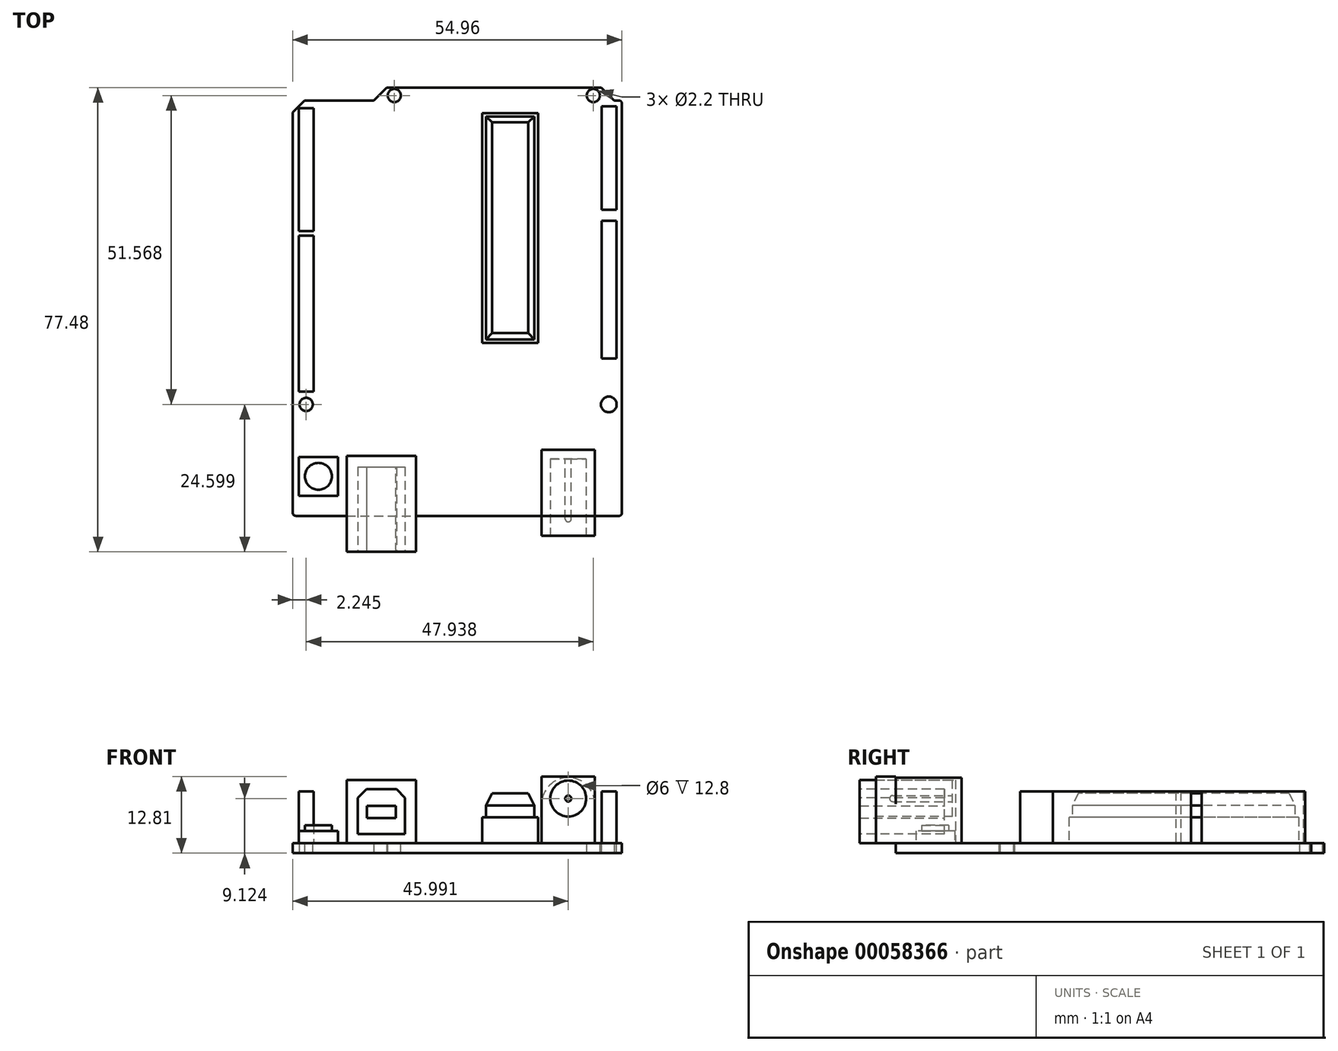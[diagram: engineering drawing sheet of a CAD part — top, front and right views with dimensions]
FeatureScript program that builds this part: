
annotation { "Feature Type Name" : "Feature", "Feature Type Description" : "" }
export const myFeature = defineFeature(function(context is Context, id is Id, definition is map)
    precondition{}
    {
        {
            var Q0;
            Q0=qCreatedBy(makeId("Top.planeOp"),FACE);
            var sketch = newSketch(context, id + "F0", { "sketchPlane" : qUnion([Q0])});
            skLineSegment(sketch, "E0.rect.bottom", {"start": v(-11.81, 35.74) * mm, "end": v(24.03, 35.74) * mm});
            skLineSegment(sketch, "E0.rect.top", {"start": v(-26.94, -35.74) * mm, "end": v(26.97, -35.74) * mm});
            skLineSegment(sketch, "E0.rect.left", {"start": v(-27.48, 31.62) * mm, "end": v(-27.48, -35.2) * mm});
            skLineSegment(sketch, "E0.rect.right", {"start": v(27.48, 33.07) * mm, "end": v(27.48, -35.23) * mm});
            skPoint(sketch, "E0.rect.middle", {"position": v(0, 0) * mm});
            skLineSegment(sketch, "E1.top", {"start": v(-25.49, 33.6) * mm, "end": v(-13.95, 33.6) * mm});
            skPoint(sketch, "E2.orphan", {"position": v(-27.48, 35.74) * mm});
            skLineSegment(sketch, "E3", {"start": v(-27.48, 31.62) * mm, "end": v(-25.49, 33.6) * mm});
            skLineSegment(sketch, "E4", {"start": v(-11.81, 35.74) * mm, "end": v(-13.95, 33.6) * mm});
            skLineSegment(sketch, "E5.top", {"start": v(26.17, 33.6) * mm, "end": v(26.94, 33.6) * mm});
            skLineSegment(sketch, "E6", {"start": v(24.03, 35.74) * mm, "end": v(26.17, 33.6) * mm});
            skPoint(sketch, "E7.orphan", {"position": v(27.48, 35.74) * mm});
            skPoint(sketch, "E8.visualSharp", {"position": v(27.48, -35.74) * mm});
            skArc(sketch, "E8.filletArc", {"start": v(26.97, -35.74) * mm, "mid": v(27.33, -35.6) * mm, "end": v(27.48, -35.23) * mm});
            skPoint(sketch, "E9.visualSharp", {"position": v(27.48, 33.6) * mm});
            skArc(sketch, "E9.filletArc", {"start": v(27.48, 33.07) * mm, "mid": v(27.32, 33.45) * mm, "end": v(26.94, 33.6) * mm});
            skPoint(sketch, "E10.visualSharp", {"position": v(-27.48, -35.74) * mm});
            skArc(sketch, "E10.filletArc", {"start": v(-27.48, -35.2) * mm, "mid": v(-27.32, -35.59) * mm, "end": v(-26.94, -35.74) * mm});
            skPoint(sketch, "E11.second.point", {"position": v(21.12, -10.57) * mm});
            skPoint(sketch, "E11.third.point", {"position": v(22.07, -8.93) * mm});
            skLineSegment(sketch, "E12", {"start": v(-13.95, 33.6) * mm, "end": v(31.22, 33.6) * mm, "construction": true});
            skSolve(sketch);
        }
        {
            var Q0;
            Q0=makeQuery(id+"F0.imprint","IMPRINT",FACE,{"disambiguationData":[TD([[makeQuery(id+"F0.imprint","IMPRINT",EDGE,{"derivedFrom":sQuery(id+"F0.wireOp",EDGE,"E0.rect.bottom")}),-1.0]])]});
            extrude(context, id + "F1", {"entities" : qUnion([Q0]), "depth" : 1.69 * mm});
        }
        {
            var Q0;
            Q0=makeQuery(id+"F1.opExtrude","CAP_FACE",FACE,{"disambiguationData":[OSD([sQuery(id+"F0.wireOp",EDGE,"E0.rect.bottom"),sQuery(id+"F0.wireOp",EDGE,"E0.rect.top"),sQuery(id+"F0.wireOp",EDGE,"E0.rect.left"),sQuery(id+"F0.wireOp",EDGE,"E0.rect.right"),sQuery(id+"F0.wireOp",EDGE,"E1.top"),sQuery(id+"F0.wireOp",EDGE,"E3"),sQuery(id+"F0.wireOp",EDGE,"E4"),sQuery(id+"F0.wireOp",EDGE,"E5.top"),sQuery(id+"F0.wireOp",EDGE,"E6"),sQuery(id+"F0.wireOp",EDGE,"E8.filletArc"),sQuery(id+"F0.wireOp",EDGE,"E9.filletArc"),sQuery(id+"F0.wireOp",EDGE,"E10.filletArc")])],"isStart":false});
            var sketch = newSketch(context, id + "F2", { "sketchPlane" : qUnion([Q0])});
            skLineSegment(sketch, "E13.top", {"start": v(24.1, -9.48) * mm, "end": v(26.53, -9.48) * mm});
            skLineSegment(sketch, "E13.left", {"start": v(24.1, 32.6) * mm, "end": v(24.1, 15.32) * mm});
            skLineSegment(sketch, "E13.right", {"start": v(26.53, 32.6) * mm, "end": v(26.53, 15.32) * mm});
            skLineSegment(sketch, "E14", {"start": v(24.1, 32.6) * mm, "end": v(26.53, 32.6) * mm});
            skLineSegment(sketch, "E15", {"start": v(24.1, 15.32) * mm, "end": v(26.53, 15.32) * mm});
            skLineSegment(sketch, "E16", {"start": v(24.1, 13.52) * mm, "end": v(26.53, 13.52) * mm});
            skLineSegment(sketch, "E17.trimOffspring", {"start": v(24.1, 13.52) * mm, "end": v(24.1, -9.48) * mm});
            skLineSegment(sketch, "E18.trimOffspring", {"start": v(26.53, 13.52) * mm, "end": v(26.53, -9.48) * mm});
            skLineSegment(sketch, "E19.bottom", {"start": v(-26.48, 32.3) * mm, "end": v(-23.98, 32.3) * mm});
            skLineSegment(sketch, "E19.top", {"start": v(-26.48, -14.99) * mm, "end": v(-23.98, -14.99) * mm});
            skLineSegment(sketch, "E19.left", {"start": v(-26.48, 32.3) * mm, "end": v(-26.48, 11.81) * mm});
            skLineSegment(sketch, "E19.right", {"start": v(-23.98, 32.3) * mm, "end": v(-23.98, 11.81) * mm});
            skLineSegment(sketch, "E20.bottom", {"start": v(-26.48, 11.81) * mm, "end": v(-23.98, 11.81) * mm});
            skLineSegment(sketch, "E20.top", {"start": v(-26.48, 11.01) * mm, "end": v(-23.98, 11.01) * mm});
            skLineSegment(sketch, "E21.trimOffspring", {"start": v(-23.98, 11.01) * mm, "end": v(-23.98, -14.99) * mm});
            skLineSegment(sketch, "E22.trimOffspring", {"start": v(-26.48, 11.01) * mm, "end": v(-26.48, -14.99) * mm});
            skSolve(sketch);
        }
        {
            var Q0;
            Q0=makeQuery(id+"F2.imprint","IMPRINT",FACE,{"disambiguationData":[TD([[makeQuery(id+"F2.imprint","IMPRINT",EDGE,{"derivedFrom":sQuery(id+"F2.wireOp",EDGE,"E13.top")}),1.0]])]});
            var Q1;
            Q1=makeQuery(id+"F2.imprint","IMPRINT",FACE,{"disambiguationData":[TD([[makeQuery(id+"F2.imprint","IMPRINT",EDGE,{"derivedFrom":sQuery(id+"F2.wireOp",EDGE,"E13.left")}),1.0]])]});
            var Q2;
            Q2=makeQuery(id+"F2.imprint","IMPRINT",FACE,{"disambiguationData":[TD([[makeQuery(id+"F2.imprint","IMPRINT",EDGE,{"derivedFrom":sQuery(id+"F2.wireOp",EDGE,"E19.bottom")}),-1.0]])]});
            var Q3;
            Q3=makeQuery(id+"F2.imprint","IMPRINT",FACE,{"disambiguationData":[TD([[makeQuery(id+"F2.imprint","IMPRINT",EDGE,{"derivedFrom":sQuery(id+"F2.wireOp",EDGE,"E19.top")}),1.0]])]});
            extrude(context, id + "F3", {"entities" : qUnion([Q0, Q1, Q2, Q3]), "depth" : 8.6 * mm});
        }
        {
            var Q0;
            Q0=makeQuery(id+"F1.opExtrude","SWEPT_FACE",FACE,{"disambiguationData":[OSD([sQuery(id+"F0.wireOp",EDGE,"E0.rect.top")])]});
            cPlane(context, id + "F4", {"entities" : qUnion([Q0]), "cplaneType" : CPlaneType.OFFSET, "offset" : 0 * mm, "width" : 150 * mm, "height" : 150 * mm});
        }
        {
            var Q0;
            Q0=qCreatedBy(id+"F4.planeOp",FACE);
            var sketch = newSketch(context, id + "F5", { "sketchPlane" : qUnion([Q0])});
            skLineSegment(sketch, "E23", {"start": v(30.92, 1.68) * mm, "end": v(22.95, 1.68) * mm, "construction": true});
            skLineSegment(sketch, "E24.bottom", {"start": v(22.95, 1.68) * mm, "end": v(14.07, 1.68) * mm});
            skLineSegment(sketch, "E24.left", {"start": v(22.95, 1.68) * mm, "end": v(22.95, 8.18) * mm});
            skLineSegment(sketch, "E24.right", {"start": v(14.07, 1.68) * mm, "end": v(14.07, 8.18) * mm});
            skArc(sketch, "E25", {"start": v(22.95, 8.18) * mm, "mid": v(18.51, 12.62) * mm, "end": v(14.07, 8.18) * mm});
            skSolve(sketch);
        }
        {
            var Q0;
            Q0=makeQuery(id+"F5.imprint","IMPRINT",FACE,{"disambiguationData":[TD([[makeQuery(id+"F5.imprint","IMPRINT",EDGE,{"derivedFrom":sQuery(id+"F5.wireOp",EDGE,"E24.bottom")}),-1.0]])]});
            extrude(context, id + "F6", {"entities" : qUnion([Q0]), "oppositeDirection" : true, "depth" : 11 * mm});
        }
        {
            var Q0;
            Q0=qCreatedBy(id+"F4.planeOp",FACE);
            var sketch = newSketch(context, id + "F7", { "sketchPlane" : qUnion([Q0])});
            skLineSegment(sketch, "E26.bottom", {"start": v(14.07, 1.69) * mm, "end": v(22.95, 1.69) * mm});
            skLineSegment(sketch, "E26.top", {"start": v(14.07, 12.81) * mm, "end": v(22.95, 12.81) * mm});
            skLineSegment(sketch, "E26.left", {"start": v(14.07, 1.69) * mm, "end": v(14.07, 12.81) * mm});
            skLineSegment(sketch, "E26.right", {"start": v(22.95, 1.69) * mm, "end": v(22.95, 12.81) * mm});
            skSolve(sketch);
        }
        {
            var Q0;
            Q0=makeQuery(id+"F7.imprint","IMPRINT",FACE,{"disambiguationData":[TD([[makeQuery(id+"F7.imprint","IMPRINT",EDGE,{"derivedFrom":sQuery(id+"F7.wireOp",EDGE,"E26.bottom")}),1.0]])]});
            extrude(context, id + "F8", {"entities" : qUnion([Q0]), "operationType" : NewBodyOperationType.ADD, "depth" : 3.3 * mm});
        }
        {
            var Q0;
            Q0=makeQuery(id+"F8.opExtrude","CAP_FACE",FACE,{"disambiguationData":[OSD([sQuery(id+"F7.wireOp",EDGE,"E26.bottom"),sQuery(id+"F7.wireOp",EDGE,"E26.top"),sQuery(id+"F7.wireOp",EDGE,"E26.left"),sQuery(id+"F7.wireOp",EDGE,"E26.right")])],"isStart":false});
            var sketch = newSketch(context, id + "F9", { "sketchPlane" : qUnion([Q0])});
            skCircle(sketch, "E27", {"center": v(18.51, 9.12) * mm, "radius": 3 * mm});
            skSolve(sketch);
        }
        {
            var Q0;
            Q0=makeQuery(id+"F9.imprint","IMPRINT",FACE,{"disambiguationData":[TD([[makeQuery(id+"F9.imprint","IMPRINT",EDGE,{"derivedFrom":sQuery(id+"F9.wireOp",EDGE,"E27")}),1.0]])]});
            var Q1;
            Q1=sQuery(id+"F9.wireOp",EDGE,"E27");
            extrude(context, id + "F10", {"entities" : qUnion([Q0]), "operationType" : NewBodyOperationType.REMOVE, "surfaceEntities" : qUnion([Q1]), "oppositeDirection" : true, "depth" : 12.8 * mm});
        }
        {
            var Q0;
            Q0=makeQuery(id+"F10.boolean.opBoolean","COPY",FACE,{"derivedFrom":makeQuery(id+"F10.opExtrude","CAP_FACE",FACE,{"disambiguationData":[OSD([sQuery(id+"F9.wireOp",EDGE,"E27")])],"isStart":false})});
            var sketch = newSketch(context, id + "F11", { "sketchPlane" : qUnion([Q0])});
            skCircle(sketch, "E28.0", {"center": v(18.51, 9.12) * mm, "radius": 3 * mm});
            skCircle(sketch, "E29", {"center": v(18.51, 9.12) * mm, "radius": 0.5 * mm});
            skSolve(sketch);
        }
        {
            var Q0;
            Q0=makeQuery(id+"F11.imprint","IMPRINT",FACE,{"disambiguationData":[TD([[makeQuery(id+"F11.imprint","IMPRINT",EDGE,{"derivedFrom":sQuery(id+"F11.wireOp",EDGE,"E29")}),1.0]])]});
            var Q1;
            Q1=sQuery(id+"F11.wireOp",EDGE,"E29");
            extrude(context, id + "F12", {"entities" : qUnion([Q0]), "surfaceEntities" : qUnion([Q1]), "depth" : 10 * mm});
        }
        {
            var Q0;
            Q0=makeQuery(id+"F1.opExtrude","CAP_FACE",FACE,{"disambiguationData":[OSD([sQuery(id+"F0.wireOp",EDGE,"E0.rect.bottom"),sQuery(id+"F0.wireOp",EDGE,"E0.rect.top"),sQuery(id+"F0.wireOp",EDGE,"E0.rect.left"),sQuery(id+"F0.wireOp",EDGE,"E0.rect.right"),sQuery(id+"F0.wireOp",EDGE,"E1.top"),sQuery(id+"F0.wireOp",EDGE,"E3"),sQuery(id+"F0.wireOp",EDGE,"E4"),sQuery(id+"F0.wireOp",EDGE,"E5.top"),sQuery(id+"F0.wireOp",EDGE,"E6"),sQuery(id+"F0.wireOp",EDGE,"E8.filletArc"),sQuery(id+"F0.wireOp",EDGE,"E9.filletArc"),sQuery(id+"F0.wireOp",EDGE,"E10.filletArc")])],"isStart":false});
            var sketch = newSketch(context, id + "F13", { "sketchPlane" : qUnion([Q0])});
            skLineSegment(sketch, "E30.bottom", {"start": v(-18.48, -35.74) * mm, "end": v(-6.88, -35.74) * mm});
            skLineSegment(sketch, "E30.top", {"start": v(-18.48, -25.74) * mm, "end": v(-6.88, -25.74) * mm});
            skLineSegment(sketch, "E30.left", {"start": v(-18.48, -35.74) * mm, "end": v(-18.48, -25.74) * mm});
            skLineSegment(sketch, "E30.right", {"start": v(-6.88, -35.74) * mm, "end": v(-6.88, -25.74) * mm});
            skSolve(sketch);
        }
        {
            var Q0;
            Q0=makeQuery(id+"F13.imprint","IMPRINT",FACE,{"disambiguationData":[TD([[makeQuery(id+"F13.imprint","IMPRINT",EDGE,{"derivedFrom":sQuery(id+"F13.wireOp",EDGE,"E30.bottom")}),1.0]])]});
            extrude(context, id + "F14", {"entities" : qUnion([Q0]), "depth" : 10.5 * mm});
        }
        {
            var Q0;
            Q0=makeQuery(id+"F14.opExtrude","SWEPT_FACE",FACE,{"disambiguationData":[OSD([sQuery(id+"F13.wireOp",EDGE,"E30.bottom")])]});
            var sketch = newSketch(context, id + "F15", { "sketchPlane" : qUnion([Q0])});
            skLineSegment(sketch, "E31.bottom", {"start": v(-18.48, 12.2) * mm, "end": v(-6.88, 12.2) * mm});
            skLineSegment(sketch, "E31.top", {"start": v(-18.48, 1.69) * mm, "end": v(-6.88, 1.69) * mm});
            skLineSegment(sketch, "E31.left", {"start": v(-18.48, 12.2) * mm, "end": v(-18.48, 1.69) * mm});
            skLineSegment(sketch, "E31.right", {"start": v(-6.88, 12.2) * mm, "end": v(-6.88, 1.69) * mm});
            skSolve(sketch);
        }
        {
            var Q0;
            Q0=makeQuery(id+"F15.imprint","IMPRINT",FACE,{"disambiguationData":[TD([[makeQuery(id+"F15.imprint","IMPRINT",EDGE,{"derivedFrom":sQuery(id+"F15.wireOp",EDGE,"E31.bottom")}),-1.0]])]});
            extrude(context, id + "F16", {"entities" : qUnion([Q0]), "operationType" : NewBodyOperationType.ADD, "depth" : 6 * mm});
        }
        {
            var Q0;
            Q0=makeQuery(id+"F16.opExtrude","CAP_FACE",FACE,{"disambiguationData":[OSD([sQuery(id+"F15.wireOp",EDGE,"E31.bottom"),sQuery(id+"F15.wireOp",EDGE,"E31.top"),sQuery(id+"F15.wireOp",EDGE,"E31.left"),sQuery(id+"F15.wireOp",EDGE,"E31.right")])],"isStart":false});
            var sketch = newSketch(context, id + "F17", { "sketchPlane" : qUnion([Q0])});
            skLineSegment(sketch, "E32.rect.bottom", {"start": v(-16.63, 3.2) * mm, "end": v(-8.73, 3.2) * mm});
            skLineSegment(sketch, "E32.rect.top", {"start": v(-15.19, 10.7) * mm, "end": v(-10.17, 10.7) * mm});
            skLineSegment(sketch, "E32.rect.left", {"start": v(-16.63, 3.2) * mm, "end": v(-16.63, 9.25) * mm});
            skLineSegment(sketch, "E32.rect.right", {"start": v(-8.73, 3.2) * mm, "end": v(-8.73, 9.25) * mm});
            skPoint(sketch, "E32.rect.middle", {"position": v(-12.68, 6.94) * mm});
            skPoint(sketch, "E32.rect.middle.positionSnap0", {"position": v(-18.48, 6.94) * mm});
            skPoint(sketch, "E32.rect.middle.positionSnap1", {"position": v(-12.68, 12.2) * mm});
            skPoint(sketch, "E32.rect.centerSnap0", {"position": v(-18.48, 6.94) * mm});
            skPoint(sketch, "E32.rect.centerSnap1", {"position": v(-12.68, 12.2) * mm});
            skLineSegment(sketch, "E33", {"start": v(-16.63, 9.25) * mm, "end": v(-15.19, 10.7) * mm});
            skLineSegment(sketch, "E34", {"start": v(-10.17, 10.7) * mm, "end": v(-8.73, 9.25) * mm});
            skPoint(sketch, "E35.orphan", {"position": v(-16.63, 10.7) * mm});
            skPoint(sketch, "E36.orphan", {"position": v(-8.73, 10.7) * mm});
            skSolve(sketch);
        }
        {
            var Q0;
            Q0=makeQuery(id+"F17.imprint","IMPRINT",FACE,{"disambiguationData":[TD([[makeQuery(id+"F17.imprint","IMPRINT",EDGE,{"derivedFrom":sQuery(id+"F17.wireOp",EDGE,"E32.rect.bottom")}),1.0]])]});
            extrude(context, id + "F18", {"entities" : qUnion([Q0]), "operationType" : NewBodyOperationType.REMOVE, "oppositeDirection" : true, "depth" : 14.14 * mm});
        }
        {
            var Q0;
            Q0=makeQuery(id+"F18.boolean.opBoolean","COPY",FACE,{"derivedFrom":makeQuery(id+"F18.opExtrude","CAP_FACE",FACE,{"disambiguationData":[OSD([sQuery(id+"F17.wireOp",EDGE,"E32.rect.bottom"),sQuery(id+"F17.wireOp",EDGE,"E32.rect.top"),sQuery(id+"F17.wireOp",EDGE,"E32.rect.left"),sQuery(id+"F17.wireOp",EDGE,"E32.rect.right"),sQuery(id+"F17.wireOp",EDGE,"E33"),sQuery(id+"F17.wireOp",EDGE,"E34")])],"isStart":false})});
            var sketch = newSketch(context, id + "F19", { "sketchPlane" : qUnion([Q0])});
            skLineSegment(sketch, "E37.rect.bottom", {"start": v(-15.12, 5.84) * mm, "end": v(-10.24, 5.84) * mm});
            skLineSegment(sketch, "E37.rect.top", {"start": v(-15.12, 7.92) * mm, "end": v(-10.24, 7.92) * mm});
            skLineSegment(sketch, "E37.rect.left", {"start": v(-15.12, 5.84) * mm, "end": v(-15.12, 7.92) * mm});
            skLineSegment(sketch, "E37.rect.right", {"start": v(-10.24, 5.84) * mm, "end": v(-10.24, 7.92) * mm});
            skPoint(sketch, "E37.rect.middle", {"position": v(-12.68, 6.88) * mm});
            skPoint(sketch, "E37.rect.middle.positionSnap0", {"position": v(-12.68, 10.7) * mm});
            skPoint(sketch, "E37.rect.centerSnap0", {"position": v(-12.68, 10.7) * mm});
            skSolve(sketch);
        }
        {
            var Q0;
            Q0=qSketchRegion(id+"F19",true);
            var Q1;
            Q1=makeQuery(id+"F16.opExtrude","CAP_FACE",FACE,{"disambiguationData":[OSD([sQuery(id+"F15.wireOp",EDGE,"E31.bottom"),sQuery(id+"F15.wireOp",EDGE,"E31.top"),sQuery(id+"F15.wireOp",EDGE,"E31.left"),sQuery(id+"F15.wireOp",EDGE,"E31.right")])],"isStart":false});
            extrude(context, id + "F20", {"entities" : qUnion([Q0]), "endBound" : BoundingType.UP_TO_SURFACE, "endBoundEntityFace" : qUnion([Q1]), "depth" : 25 * mm});
        }
        {
            var Q0;
            Q0=makeQuery(id+"F1.opExtrude","CAP_FACE",FACE,{"disambiguationData":[OSD([sQuery(id+"F0.wireOp",EDGE,"E0.rect.bottom"),sQuery(id+"F0.wireOp",EDGE,"E0.rect.top"),sQuery(id+"F0.wireOp",EDGE,"E0.rect.left"),sQuery(id+"F0.wireOp",EDGE,"E0.rect.right"),sQuery(id+"F0.wireOp",EDGE,"E1.top"),sQuery(id+"F0.wireOp",EDGE,"E3"),sQuery(id+"F0.wireOp",EDGE,"E4"),sQuery(id+"F0.wireOp",EDGE,"E5.top"),sQuery(id+"F0.wireOp",EDGE,"E6"),sQuery(id+"F0.wireOp",EDGE,"E8.filletArc"),sQuery(id+"F0.wireOp",EDGE,"E9.filletArc"),sQuery(id+"F0.wireOp",EDGE,"E10.filletArc")])],"isStart":false});
            var sketch = newSketch(context, id + "F21", { "sketchPlane" : qUnion([Q0])});
            skLineSegment(sketch, "E38.rect.bottom", {"start": v(-26.44, -25.9) * mm, "end": v(-19.94, -25.9) * mm});
            skLineSegment(sketch, "E38.rect.top", {"start": v(-26.44, -32.4) * mm, "end": v(-19.94, -32.4) * mm});
            skLineSegment(sketch, "E38.rect.left", {"start": v(-26.44, -25.9) * mm, "end": v(-26.44, -32.4) * mm});
            skLineSegment(sketch, "E38.rect.right", {"start": v(-19.94, -25.9) * mm, "end": v(-19.94, -32.4) * mm});
            skPoint(sketch, "E38.rect.middle", {"position": v(-23.19, -29.14) * mm});
            skSolve(sketch);
        }
        {
            var Q0;
            Q0=makeQuery(id+"F21.imprint","IMPRINT",FACE,{"disambiguationData":[TD([[makeQuery(id+"F21.imprint","IMPRINT",EDGE,{"derivedFrom":sQuery(id+"F21.wireOp",EDGE,"E38.rect.bottom")}),-1.0]])]});
            extrude(context, id + "F22", {"entities" : qUnion([Q0]), "depth" : 2 * mm});
        }
        {
            var Q0;
            Q0=makeQuery(id+"F22.opExtrude","CAP_FACE",FACE,{"disambiguationData":[OSD([sQuery(id+"F21.wireOp",EDGE,"E38.rect.bottom"),sQuery(id+"F21.wireOp",EDGE,"E38.rect.top"),sQuery(id+"F21.wireOp",EDGE,"E38.rect.left"),sQuery(id+"F21.wireOp",EDGE,"E38.rect.right")])],"isStart":false});
            var sketch = newSketch(context, id + "F23", { "sketchPlane" : qUnion([Q0])});
            skCircle(sketch, "E39", {"center": v(-23.19, -29.14) * mm, "radius": 2.24 * mm});
            skPoint(sketch, "E39.centerSnap0", {"position": v(-26.44, -29.14) * mm});
            skSolve(sketch);
        }
        {
            var Q0;
            Q0=makeQuery(id+"F23.imprint","IMPRINT",FACE,{"disambiguationData":[TD([[makeQuery(id+"F23.imprint","IMPRINT",EDGE,{"derivedFrom":sQuery(id+"F23.wireOp",EDGE,"E39")}),1.0]])]});
            extrude(context, id + "F24", {"entities" : qUnion([Q0]), "depth" : 1 * mm});
        }
        {
            var Q0;
            Q0=makeQuery(id+"F1.opExtrude","CAP_FACE",FACE,{"disambiguationData":[OSD([sQuery(id+"F0.wireOp",EDGE,"E0.rect.bottom"),sQuery(id+"F0.wireOp",EDGE,"E0.rect.top"),sQuery(id+"F0.wireOp",EDGE,"E0.rect.left"),sQuery(id+"F0.wireOp",EDGE,"E0.rect.right"),sQuery(id+"F0.wireOp",EDGE,"E1.top"),sQuery(id+"F0.wireOp",EDGE,"E3"),sQuery(id+"F0.wireOp",EDGE,"E4"),sQuery(id+"F0.wireOp",EDGE,"E5.top"),sQuery(id+"F0.wireOp",EDGE,"E6"),sQuery(id+"F0.wireOp",EDGE,"E8.filletArc"),sQuery(id+"F0.wireOp",EDGE,"E9.filletArc"),sQuery(id+"F0.wireOp",EDGE,"E10.filletArc")])],"isStart":false});
            var sketch = newSketch(context, id + "F25", { "sketchPlane" : qUnion([Q0])});
            skLineSegment(sketch, "E40.bottom", {"start": v(13.47, 31.5) * mm, "end": v(4.14, 31.5) * mm});
            skLineSegment(sketch, "E40.top", {"start": v(13.47, -6.87) * mm, "end": v(4.14, -6.87) * mm});
            skLineSegment(sketch, "E40.left", {"start": v(13.47, 31.5) * mm, "end": v(13.47, -6.87) * mm});
            skLineSegment(sketch, "E40.right", {"start": v(4.14, 31.5) * mm, "end": v(4.14, -6.87) * mm});
            skSolve(sketch);
        }
        {
            var Q0;
            Q0=makeQuery(id+"F25.imprint","IMPRINT",FACE,{"disambiguationData":[TD([[makeQuery(id+"F25.imprint","IMPRINT",EDGE,{"derivedFrom":sQuery(id+"F25.wireOp",EDGE,"E40.bottom")}),1.0]])]});
            extrude(context, id + "F26", {"entities" : qUnion([Q0]), "depth" : 4.3 * mm});
        }
        {
            var Q0;
            Q0=makeQuery(id+"F26.opExtrude","CAP_FACE",FACE,{"disambiguationData":[OSD([sQuery(id+"F25.wireOp",EDGE,"E40.bottom"),sQuery(id+"F25.wireOp",EDGE,"E40.top"),sQuery(id+"F25.wireOp",EDGE,"E40.left"),sQuery(id+"F25.wireOp",EDGE,"E40.right")])],"isStart":false});
            var sketch = newSketch(context, id + "F27", { "sketchPlane" : qUnion([Q0])});
            skLineSegment(sketch, "E41.rect.bottom", {"start": v(4.76, 30.91) * mm, "end": v(12.84, 30.91) * mm});
            skLineSegment(sketch, "E41.rect.top", {"start": v(4.76, -6.28) * mm, "end": v(12.84, -6.28) * mm});
            skLineSegment(sketch, "E41.rect.left", {"start": v(4.76, 30.91) * mm, "end": v(4.76, -6.28) * mm});
            skLineSegment(sketch, "E41.rect.right", {"start": v(12.84, 30.91) * mm, "end": v(12.84, -6.28) * mm});
            skPoint(sketch, "E41.rect.middle", {"position": v(8.8, 12.32) * mm});
            skPoint(sketch, "E41.rect.middle.positionSnap0", {"position": v(8.8, 31.5) * mm});
            skPoint(sketch, "E41.rect.middle.positionSnap1", {"position": v(4.14, 12.32) * mm});
            skPoint(sketch, "E41.rect.centerSnap0", {"position": v(8.8, 31.5) * mm});
            skPoint(sketch, "E41.rect.centerSnap1", {"position": v(4.14, 12.32) * mm});
            skSolve(sketch);
        }
        {
            var Q0;
            Q0=makeQuery(id+"F27.imprint","IMPRINT",FACE,{"disambiguationData":[TD([[makeQuery(id+"F27.imprint","IMPRINT",EDGE,{"derivedFrom":sQuery(id+"F27.wireOp",EDGE,"E41.rect.bottom")}),-1.0]])]});
            extrude(context, id + "F28", {"entities" : qUnion([Q0]), "depth" : 2 * mm});
        }
        {
            var Q0;
            Q0=makeQuery(id+"F28.opExtrude","CAP_FACE",FACE,{"disambiguationData":[OSD([sQuery(id+"F27.wireOp",EDGE,"E41.rect.bottom"),sQuery(id+"F27.wireOp",EDGE,"E41.rect.top"),sQuery(id+"F27.wireOp",EDGE,"E41.rect.left"),sQuery(id+"F27.wireOp",EDGE,"E41.rect.right")])],"isStart":false});
            cPlane(context, id + "F29", {"entities" : qUnion([Q0]), "cplaneType" : CPlaneType.OFFSET, "offset" : 2 * mm, "width" : 150 * mm, "height" : 150 * mm});
        }
        {
            var Q0;
            Q0=qCreatedBy(id+"F29.planeOp",FACE);
            var sketch = newSketch(context, id + "F30", { "sketchPlane" : qUnion([Q0])});
            skLineSegment(sketch, "E42.bottom", {"start": v(5.78, 29.94) * mm, "end": v(11.83, 29.94) * mm});
            skLineSegment(sketch, "E42.top", {"start": v(5.78, -5.22) * mm, "end": v(11.83, -5.22) * mm});
            skLineSegment(sketch, "E42.left", {"start": v(5.78, 29.94) * mm, "end": v(5.78, -5.22) * mm});
            skLineSegment(sketch, "E42.right", {"start": v(11.83, 29.94) * mm, "end": v(11.83, -5.22) * mm});
            skSolve(sketch);
        }
        {
            var Q1;
            Q1=makeQuery(id+"F30.imprint","IMPRINT",FACE,{"disambiguationData":[TD([[makeQuery(id+"F30.imprint","IMPRINT",EDGE,{"derivedFrom":sQuery(id+"F30.wireOp",EDGE,"E42.bottom")}),-1.0]])]});
            var Q2;
            Q2=makeQuery(id+"F28.opExtrude","CAP_FACE",FACE,{"disambiguationData":[OSD([sQuery(id+"F27.wireOp",EDGE,"E41.rect.bottom"),sQuery(id+"F27.wireOp",EDGE,"E41.rect.top"),sQuery(id+"F27.wireOp",EDGE,"E41.rect.left"),sQuery(id+"F27.wireOp",EDGE,"E41.rect.right")])],"isStart":false});
            loft(context, id + "F31", {"sheetProfilesArray" : [{ "sheetProfileEntities" : qUnion([Q1]) }, { "sheetProfileEntities" : qUnion([Q2]) }]});
        }
        {
            var Q0;
            Q0=makeQuery(id+"F1.opExtrude","CAP_FACE",FACE,{"disambiguationData":[OSD([sQuery(id+"F0.wireOp",EDGE,"E0.rect.bottom"),sQuery(id+"F0.wireOp",EDGE,"E0.rect.top"),sQuery(id+"F0.wireOp",EDGE,"E0.rect.left"),sQuery(id+"F0.wireOp",EDGE,"E0.rect.right"),sQuery(id+"F0.wireOp",EDGE,"E1.top"),sQuery(id+"F0.wireOp",EDGE,"E3"),sQuery(id+"F0.wireOp",EDGE,"E4"),sQuery(id+"F0.wireOp",EDGE,"E5.top"),sQuery(id+"F0.wireOp",EDGE,"E6"),sQuery(id+"F0.wireOp",EDGE,"E8.filletArc"),sQuery(id+"F0.wireOp",EDGE,"E9.filletArc"),sQuery(id+"F0.wireOp",EDGE,"E10.filletArc")])],"isStart":false});
            var sketch = newSketch(context, id + "F32", { "sketchPlane" : qUnion([Q0])});
            skCircle(sketch, "E43", {"center": v(-10.52, 34.43) * mm, "radius": 1.1 * mm});
            skCircle(sketch, "E44", {"center": v(22.7, 34.43) * mm, "radius": 1.1 * mm});
            skSolve(sketch);
        }
        {
            var Q0;
            Q0=makeQuery(id+"F32.imprint","IMPRINT",FACE,{"disambiguationData":[TD([[makeQuery(id+"F32.imprint","IMPRINT",EDGE,{"derivedFrom":sQuery(id+"F32.wireOp",EDGE,"E43")}),1.0]])]});
            var Q1;
            Q1=makeQuery(id+"F32.imprint","IMPRINT",FACE,{"disambiguationData":[TD([[makeQuery(id+"F32.imprint","IMPRINT",EDGE,{"derivedFrom":sQuery(id+"F32.wireOp",EDGE,"E44")}),1.0]])]});
            extrude(context, id + "F33", {"entities" : qUnion([Q0, Q1]), "operationType" : NewBodyOperationType.REMOVE, "endBound" : BoundingType.THROUGH_ALL, "oppositeDirection" : true, "depth" : 25 * mm});
        }
        {
            var Q0;
            Q0=makeQuery(id+"F1.opExtrude","CAP_FACE",FACE,{"disambiguationData":[OSD([sQuery(id+"F0.wireOp",EDGE,"E0.rect.bottom"),sQuery(id+"F0.wireOp",EDGE,"E0.rect.top"),sQuery(id+"F0.wireOp",EDGE,"E0.rect.left"),sQuery(id+"F0.wireOp",EDGE,"E0.rect.right"),sQuery(id+"F0.wireOp",EDGE,"E1.top"),sQuery(id+"F0.wireOp",EDGE,"E3"),sQuery(id+"F0.wireOp",EDGE,"E4"),sQuery(id+"F0.wireOp",EDGE,"E5.top"),sQuery(id+"F0.wireOp",EDGE,"E6"),sQuery(id+"F0.wireOp",EDGE,"E8.filletArc"),sQuery(id+"F0.wireOp",EDGE,"E9.filletArc"),sQuery(id+"F0.wireOp",EDGE,"E10.filletArc")])],"isStart":false});
            var sketch = newSketch(context, id + "F34", { "sketchPlane" : qUnion([Q0])});
            skCircle(sketch, "E45", {"center": v(-25.23, -17.14) * mm, "radius": 1.1 * mm});
            skCircle(sketch, "E46", {"center": v(25.28, -17.14) * mm, "radius": 1.31 * mm});
            skSolve(sketch);
        }
        {
            var Q0;
            Q0=makeQuery(id+"F34.imprint","IMPRINT",FACE,{"disambiguationData":[TD([[makeQuery(id+"F34.imprint","IMPRINT",EDGE,{"derivedFrom":sQuery(id+"F34.wireOp",EDGE,"E45")}),1.0]])]});
            var Q1;
            Q1=makeQuery(id+"F34.imprint","IMPRINT",FACE,{"disambiguationData":[TD([[makeQuery(id+"F34.imprint","IMPRINT",EDGE,{"derivedFrom":sQuery(id+"F34.wireOp",EDGE,"E46")}),1.0]])]});
            var Q2;
            Q2=sQuery(id+"F34.wireOp",EDGE,"E45");
            var Q3;
            Q3=sQuery(id+"F34.wireOp",EDGE,"E46");
            extrude(context, id + "F35", {"entities" : qUnion([Q0, Q1]), "operationType" : NewBodyOperationType.REMOVE, "surfaceEntities" : qUnion([Q2, Q3]), "endBound" : BoundingType.THROUGH_ALL, "oppositeDirection" : true, "depth" : 25 * mm});
        }
        {
            var Q0;
            Q0=makeQuery(id+"F12.opExtrude","CAP_FACE",FACE,{"disambiguationData":[OSD([sQuery(id+"F11.wireOp",EDGE,"E29")])],"isStart":false});
            var sketch = newSketch(context, id + "F36", { "sketchPlane" : qUnion([Q0])});
            skArc(sketch, "E47.0", {"start": v(18.51, 9.62) * mm, "mid": v(18.01, 9.12) * mm, "end": v(18.51, 8.62) * mm});
            skLineSegment(sketch, "E48", {"start": v(18.51, 9.62) * mm, "end": v(18.51, 8.62) * mm});
            skSolve(sketch);
        }
        {
            var Q0;
            {var subQ2=sQuery(id+"F36.wireOp",EDGE,"E48");Q0=makeQuery(id+"F36.imprint","IMPRINT",FACE,{"disambiguationData":[TD([[makeQuery(id+"F36.imprint","IMPRINT",EDGE,{"derivedFrom":subQ2}),1.0]])]});}
            var Q1;
            Q1=sQuery(id+"F36.wireOp",EDGE,"E48");
            revolve(context, id + "F37", {"operationType" : NewBodyOperationType.ADD, "entities" : qUnion([Q0]), "axis" : qUnion([Q1]), "revolveType" : RevolveType.ONE_DIRECTION, "angle" : 180 * degree});
        }
    });
